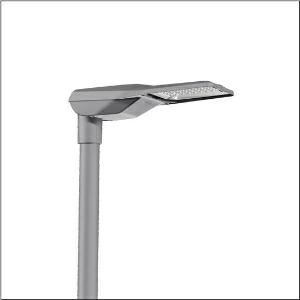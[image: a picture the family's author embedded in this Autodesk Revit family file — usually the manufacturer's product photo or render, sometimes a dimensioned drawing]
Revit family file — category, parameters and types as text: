
# Revit family: streetlight_sl_21_iq_mini___st1_0a_5xe2d31d08hb_45ae
name_source: partatom
category: Lighting Fixtures
units: mm (PartAtom-declared; Revit-internal decimal feet)

## family parameters
Cut with Voids When Loaded = No
Host = Face
Light Source = No
Part Type = Normal
Room Calculation Point = No
Round Connector Dimension = Use Diameter
Shared = No

## types (1)
- --- (1 x LED, 9450 lm, 70.9 W, 3000K)
    Apparent Load = 71 VA
    CIE Flux Codes = 37 72 97 100 100
    Color Rendering = 70
    Color Temperature = 3000K
    Default Elevation = 1800 mm
    Description = Streetlight SL 21 iQ mini, mast luminaire, primary light control with lens, of PMMA, primary optical cover: cover, of toughened safety glass, transparent, light distribution: ST1.0a, light emission: direct distribution, primary light characteristic: asymmetric, installation type: post-top, side-entry, LED, High Power LED, rated luminous flux: 9.450lm, luminous efficacy: 133lm/W, light colour: 730, colour temperature: 3000K, control: Auto-Match, Temp-Guard, Lumen-Switch, Night-Set, Smart-Wire, Light-Fading, Desk-Remote (wireless, voltage-free reading and setting of iQ features in the workshop via application-optimized NFC function/RFID function), optimised constant luminous flux control (CLO 2.0), presetting dimming linear, mains connection: 220..240V, AC, 50/60Hz, start of lifetime: 71W, end of service life: 75W, reduction: 31W, luminaire housing, of diecast aluminium, powder-coated, Siteco® metallic grey (DB 702S), corrosivity category C5 mid according to DIN EN ISO 12944, please order mast flange separately, inclination adjustable: 0°, 5°, 10°, 15°, sealing non-destructively replaceable, multi-level sealing system, length: 628mm, width: 235mm, height: 110mm, mast flange for spigot size: 42mm (side-entry): 5XC10008XM4, 60/48mm (side-entry/post-top): 5XC10108XM2, 76/60mm (side-entry/post-top): 5XC10108XM1, protection rating (complete): IP66, insulation class (complete): insulation class II (safety insulation), certification: CE, ENEC, ENEC+, VDE, impact resistance: IK09, permissible operating ambient temperature for outdoor applications: -40..+50°C, standard-compliant lighting for roads and squares, packaging unit: 1 piece

Light Distribution: ST1.0a
    Height = 110 mm
    Lamp = 1 x LED
    Lamp Light Flux = 9450 lm
    Lamp Power = 70.9 W
    Lamp count = 1
    Length = 625 mm
    Luminous efficacy = 133 lm/W
    Manufacturer = Siteco
    ModVariant = No
    Model = 5XE2D31D08HB
    Number of Poles = 1
    OnlyDefault = Yes
    Power Factor = 1
    Product Name = Streetlight SL 21 iQ mini | ST1.0a
    Product group = mast luminaire | pylon top
    ProductGroupID = 6100
    Protection Class = Protection class II
    Protection Degree = IP 66
    RLX_Detail_Level = 1
    RLX_Emergency_Light_Flux = 0 lm
    RLX_Emergency_Type = 0
    RLX_Emergency_Type_DB = No
    RlxData = <blob elided: 92145 chars, md5=b65bdbe6>
    Socket = socket
    Standby Power = 0 W
    System Light Flux = 9450 lm
    System Power = 71 W
    Type Comments = factory setting: luminous flux: 100 % | dim-lin: 254 | 711 mA
    Type Image = l_1003519.jpg
    URL = http://relux.com
    VarID = @adj_090495
    Voltage = 0 V
    Weight = 0.00 kg
    Width = 234 mm

## geometry (parser evidence)
native form markers: Blend x4, Sweep x9
no freeform markers — native parametric forms only
